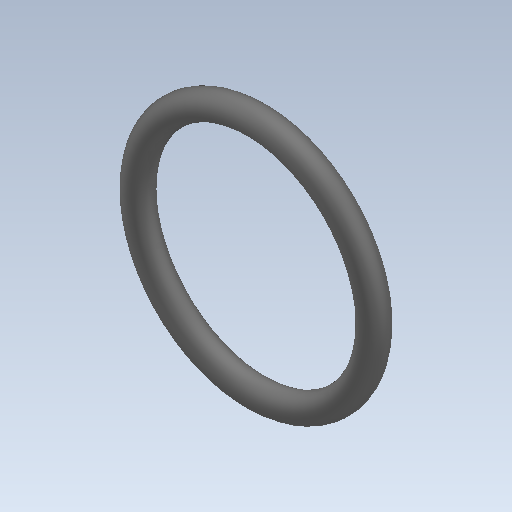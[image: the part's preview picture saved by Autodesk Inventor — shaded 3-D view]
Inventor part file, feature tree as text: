
AUTODESK INVENTOR PART (.ipt)
format: ipt  version: 2020 (Build 240168000, 168)  size: 134,656 bytes
history: native  units: in
note: dims shown in document units (in); Inventor stores cm internally (conversion verified against a paired STEP export)
features: revolve x1
ambient origin geometry x8: Origin, YZ Plane, XZ Plane, XY Plane, X Axis, Y Axis, Z Axis, Center Point
bodies: Solid1 (feature_tree)
feature tree (1):
  revolve  "Revolve1"  [1 undecoded]
note: 1 required parameter value undecoded (feature->parameter linkage not recoverable at this tier; creation-order binding heuristic only, values carry confidence <= 0.55)
